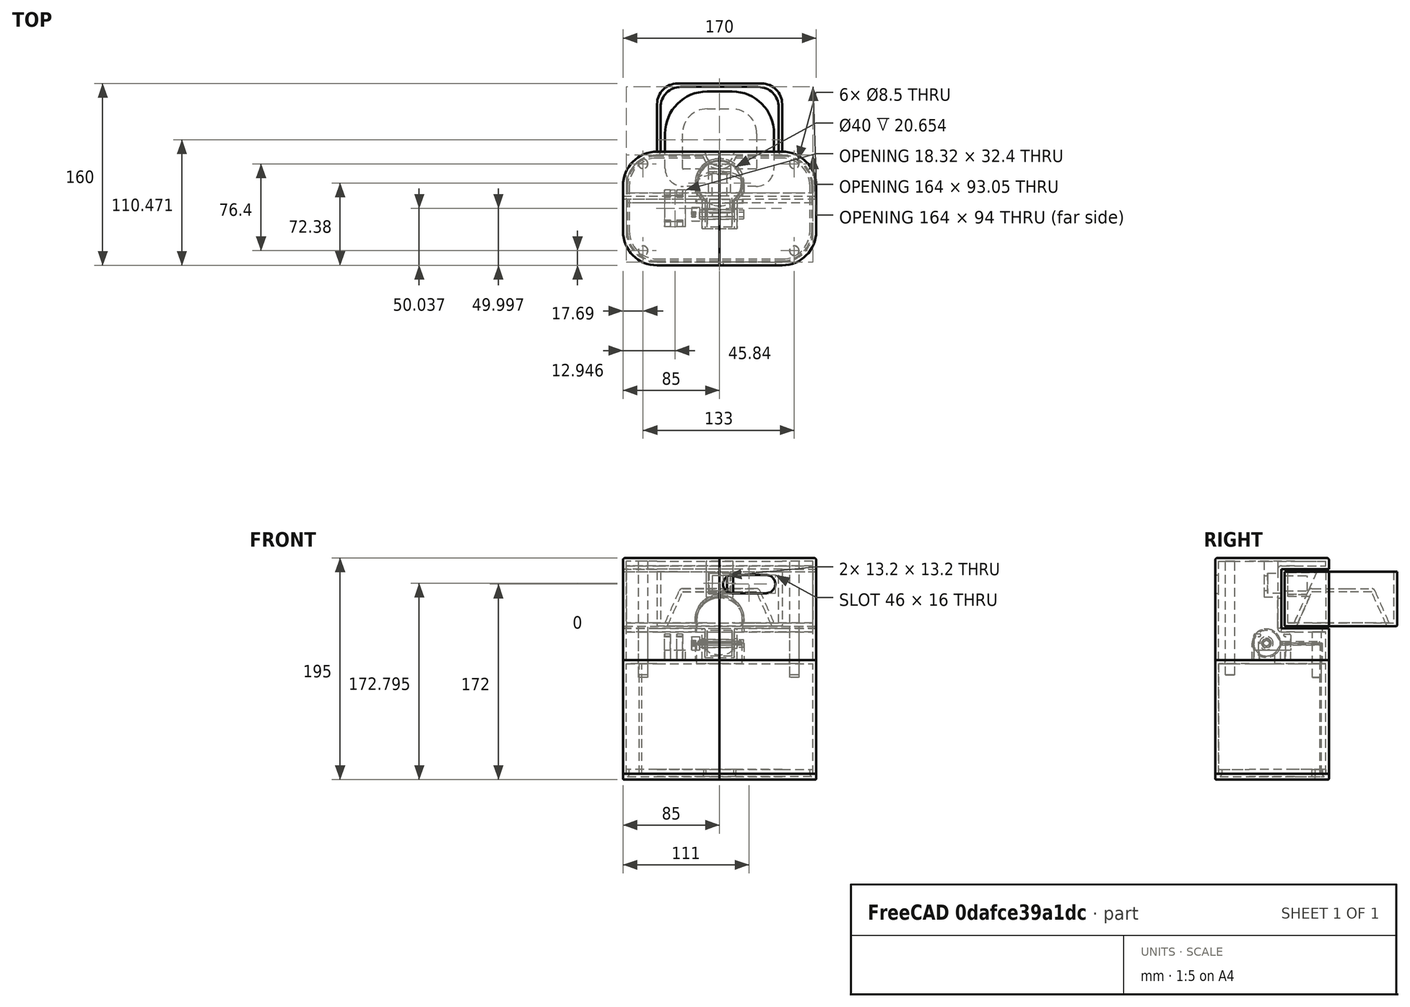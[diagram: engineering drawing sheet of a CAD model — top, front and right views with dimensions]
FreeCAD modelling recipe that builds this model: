
FCSTD DOCUMENT  (FreeCAD 1.0R39109 (Git))
Label: Feeder V3
License: All rights reserved
LicenseURL: https://en.wikipedia.org/wiki/All_rights_reserved
objects: Sketcher::SketchObject×29, PartDesign::Pocket×19, PartDesign::Pad×17, PartDesign::Fillet×8, PartDesign::ShapeBinder×8, PartDesign::Body×6, App::Link×6, PartDesign::Plane×5, PartDesign::SubShapeBinder×5, PartDesign::Thickness×4, PartDesign::Line×2, PartDesign::PolarPattern×1, PartDesign::LinearPattern×1, PartDesign::Point×1, PartDesign::Revolution×1, Part::Compound×1, Part::Box×1, Part::Cut×1, Measure::MeasureLength×1, App::DocumentObjectGroup×1
note: 239 computed .brp shape members not serialized (recipe doc carries the construction recipe); baked Part::Feature solids carry a one-line shape summary decoded from their .brp

FEATURE [Sketcher::SketchObject] Sketch
  ArcFitTolerance = 1e-06
  AttachmentSupport = -> [XY_Plane]
  FullyConstrained = true
  MakeInternals = false
  MapMode = 5
  sketch-geometry (4):
    g0: LineSegment StartX=-85 StartY=-72.3831 StartZ=0 EndX=85 EndY=-72.3831 EndZ=0
    g1: LineSegment StartX=85 StartY=-72.3831 StartZ=0 EndX=85 EndY=27.6169 EndZ=0
    g2: LineSegment StartX=85 StartY=27.6169 StartZ=0 EndX=-85 EndY=27.6169 EndZ=0
    g3: LineSegment StartX=-85 StartY=27.6169 StartZ=0 EndX=-85 EndY=-72.3831 EndZ=0
  constraints (11):
    c: Coincident(g0,g1)
    c: Coincident(g1,g2)
    c: Coincident(g2,g3)
    c: Coincident(g3,g0)
    c: Horizontal(g0)
    c: Vertical(g1)
    c: Vertical(g3)
    c: Distance(g1,g3) = 170
    c: Distance(g0,g2) = 100
    c: Symmetric(g2,g1,g-2)
    c: Block(g2)
FEATURE [PartDesign::Pad] Pad  label="Base"
  Direction = (0,0,1)
  Length = 200
  Length2 = 10
  Profile = -> Sketch
  ReferenceAxis = -> Sketch [N_Axis]
  Refine = true
  Suppressed = false
  Type = 0
FEATURE [PartDesign::Fillet] Fillet  label="Round Base Corner"
  Base = -> Pad [Edge1,Edge8,Edge2,Edge5]
  BaseFeature = -> Pad
  Radius = 30
  Refine = true
  SupportTransform = false
  Suppressed = false
  UseAllEdges = false
FEATURE [PartDesign::Thickness] Thickness
  Base = -> Fillet [Face2]
  BaseFeature = -> Fillet
  Intersection = false
  Join = 0
  Mode = 0
  Refine = true
  Reversed = true
  SupportTransform = false
  Suppressed = false
  Value = 3
FEATURE [Sketcher::SketchObject] Sketch001
  ArcFitTolerance = 1e-06
  AttachmentSupport = -> [Thickness]
  ExternalGeometry = -> [Thickness]
  FullyConstrained = true
  MakeInternals = false
  MapMode = 5
  Placement = pos=(0,0,200) rot=(0,0,1;0rad)
  sketch-geometry (7):
    g0: ArcOfCircle CenterX=0 CenterY=0 CenterZ=0 NormalX=0 NormalY=0 NormalZ=1 AngleXU=0 Radius=21.5 StartAngle=5.54716 EndAngle=10.1608
    g1: Circle CenterX=0 CenterY=0 CenterZ=0 NormalX=0 NormalY=0 NormalZ=1 AngleXU=0 Radius=20
    g2: LineSegment StartX=15.9346 StartY=-14.434 StartZ=0 EndX=15.5 EndY=-14.9137 EndZ=0
    g3: LineSegment StartX=-15.9344 StartY=-14.4341 StartZ=0 EndX=-15.5 EndY=-14.9137 EndZ=0
    g4: LineSegment StartX=-15.5 StartY=-14.9137 StartZ=0 EndX=-15.5 EndY=-39.9137 EndZ=0
    g5: LineSegment StartX=15.5 StartY=-14.9137 StartZ=0 EndX=15.5 EndY=-39.9137 EndZ=0
    g6: LineSegment StartX=-15.5 StartY=-39.9137 StartZ=0 EndX=15.5 EndY=-39.9137 EndZ=0
  constraints (16):
    c: Block(g1)
    c: Block(g0)
    c: Tangent(g0,g3) = -1.5708
    c: Tangent(g0,g2) = 1.5708
    c: Distance(g4) = 25
    c: Vertical(g4)
    c: Coincident(g4,g3)
    c: Vertical(g5)
    c: Coincident(g5,g2)
    c: Coincident(g6,g4)
    c: Coincident(g6,g5)
    c: Horizontal(g6)
    c: Diameter(g1) = 40
    c: Radius(g0) = 21.5
    c: DistanceY(g5,g5) = 25
    c: DistanceX(g6,g6) = 31
FEATURE [PartDesign::Pad] Pad001  label="DoorWay"
  BaseFeature = -> Thickness
  Direction = (0,0,1)
  Length = 15
  Length2 = 10
  Profile = -> Sketch001
  ReferenceAxis = -> Sketch001 [N_Axis]
  Refine = true
  Suppressed = false
  Type = 0
FEATURE [Sketcher::SketchObject] Sketch003
  ArcFitTolerance = 1e-06
  AttachmentSupport = -> [Pad001]
  ExternalGeometry = -> [Pad001]
  FullyConstrained = true
  MakeInternals = false
  MapMode = 5
  Placement = pos=(-15.5,0,0) rot=(0.57735,-0.57735,-0.57735;2.0944rad)
  sketch-geometry (3):
    g0: ArcOfCircle CenterX=27.4137 CenterY=215 CenterZ=0 NormalX=0 NormalY=0 NormalZ=1 AngleXU=0 Radius=12.5 StartAngle=-4.35e-14 EndAngle=3.14159
    g1: LineSegment StartX=14.9137 StartY=215 StartZ=0 EndX=27.4137 EndY=215 EndZ=0
    g2: LineSegment StartX=39.9137 StartY=215 StartZ=0 EndX=27.4137 EndY=215 EndZ=0
  constraints (9):
    c: Coincident(g0,g-3)
    c: Coincident(g0,g-3)
    c: PointOnObject(g0,g-3)
    c: PointOnObject(g1,g0)
    c: Coincident(g1,g0)
    c: Horizontal(g1)
    c: PointOnObject(g2,g0)
    c: Coincident(g2,g0)
    c: Horizontal(g2)
FEATURE [PartDesign::Pad] Pad002  label="Door Hinge Form"
  BaseFeature = -> Pad001
  Direction = (-1,0,0)
  Length = 25
  Length2 = 10
  Profile = -> Sketch003
  ReferenceAxis = -> Sketch003 [N_Axis]
  Refine = true
  Suppressed = false
  Type = 3
  UpToFace = -> Pad001 [Face23]
FEATURE [PartDesign::Pocket] Pocket  label="Pocket Container"
  BaseFeature = -> Pad002
  Direction = (0,0,-1)
  Length = 5
  Length2 = 5
  Midplane = true
  Profile = -> Pad002 [Face28]
  Refine = true
  Suppressed = false
  Type = 1
FEATURE [Sketcher::SketchObject] Sketch004
  ArcFitTolerance = 1e-06
  AttachmentSupport = -> [Pocket]
  ExternalGeometry = -> [Pocket]
  FullyConstrained = true
  MakeInternals = false
  MapMode = 5
  Placement = pos=(15.5,0,0) rot=(0.57735,0.57735,0.57735;2.0944rad)
  sketch-geometry (1):
    g0: Circle CenterX=-27.4137 CenterY=215 CenterZ=0 NormalX=0 NormalY=0 NormalZ=1 AngleXU=0 Radius=4.25
  constraints (2):
    c: Diameter(g0) = 8.5
    c: Coincident(g0,g-3)
FEATURE [PartDesign::Pocket] Pocket001  label="Pocket Hinge Circle"
  BaseFeature = -> Pocket
  Direction = (-1,0,0)
  Length = 5
  Length2 = 5
  Profile = -> Sketch004 [Edge1]
  ReferenceAxis = -> Sketch004 [N_Axis]
  Refine = true
  Suppressed = false
  Type = 1
FEATURE [Sketcher::SketchObject] Sketch009
  ArcFitTolerance = 1e-06
  AttachmentSupport = -> [YZ_Plane]
  ExternalGeometry = -> [Pocket001]
  FullyConstrained = true
  MakeInternals = false
  MapMode = 5
  Placement = pos=(0,0,0) rot=(0.57735,0.57735,0.57735;2.0944rad)
  sketch-geometry (1):
    g0: Circle CenterX=-27.4137 CenterY=215 CenterZ=0 NormalX=0 NormalY=0 NormalZ=1 AngleXU=0 Radius=12.5
  constraints (3):
    c: DistanceX(g-4,g-5) = 25
    c: Coincident(g0,g-3)
    c: PointOnObject(g-5,g0)
FEATURE [PartDesign::Pocket] Pocket004  label="Pocket Doorway form"
  BaseFeature = -> Pocket001
  Direction = (-1,0,0)
  Length = 26
  Length2 = 5
  Midplane = true
  Profile = -> Sketch009
  ReferenceAxis = -> Sketch009 [N_Axis]
  Refine = true
  Suppressed = false
  Type = 0
FEATURE [PartDesign::Line] DatumLine  label="Hinge center"
  AttacherType = Attacher::AttachEngineLine
  AttachmentSupport = -> [Pocket004]
  Length = 20
  MapMode = 42
  Placement = pos=(0,-27.4425,215) rot=(0.57735,0.57735,0.57735;2.0944rad)
  ResizeMode = 0
FEATURE [PartDesign::Plane] DatumPlane  label="Door floor plane"
  AttachmentSupport = -> [DatumLine]
  Length = 62.6838
  MapMode = 3
  Placement = pos=(0,-27.4425,215) rot=(0.707107,0.707107,0;3.14159rad)
  ResizeMode = 0
  Width = 60.2413
FEATURE [PartDesign::Plane] CopyDatumPlane
  Length = 62.6838
  Placement = pos=(-2.6041e-12,-27.4425,215) rot=(0.707107,0.707107,0;3.14159rad)
  ResizeMode = 0
  Width = 60.2413
FEATURE [PartDesign::SubShapeBinder] Binder
  BindCopyOnChange = 0
  BindMode = 0
  ClaimChildren = false
  Context = -> Body001 [Binder.]
  Fuse = false
  MakeFace = true
  OffsetFill = false
  OffsetIntersection = false
  OffsetJoinType = 0
  OffsetOpenResult = false
  PartialLoad = false
  Refine = true
  Relative = true
  Support = -> [Body[Pocket004.Edge74,Pocket004.Face29,Pocket004.Face33,Pocket004.Edge73]]
  _Version = 2
FEATURE [Sketcher::SketchObject] Sketch011
  ArcFitTolerance = 1e-06
  AttachmentSupport = -> [Binder]
  ExternalGeometry = -> [Binder]
  FullyConstrained = true
  MakeInternals = false
  MapMode = 5
  Placement = pos=(-13,0,0) rot=(0.57735,0.57735,0.57735;2.0944rad)
  sketch-geometry (7):
    g0: LineSegment StartX=-31.6637 StartY=215 StartZ=0 EndX=-29.5387 EndY=211.319 EndZ=0
    g1: LineSegment StartX=-29.5387 StartY=211.319 StartZ=0 EndX=-25.2887 EndY=211.319 EndZ=0
    g2: LineSegment StartX=-25.2887 StartY=211.319 StartZ=0 EndX=-23.1637 EndY=215 EndZ=0
    g3: LineSegment StartX=-23.1637 StartY=215 StartZ=0 EndX=-25.2887 EndY=218.681 EndZ=0
    g4: LineSegment StartX=-25.2887 StartY=218.681 StartZ=0 EndX=-29.5387 EndY=218.681 EndZ=0
    g5: LineSegment StartX=-29.5387 StartY=218.681 StartZ=0 EndX=-31.6637 EndY=215 EndZ=0
    g6: Circle [constr] CenterX=-27.4137 CenterY=215 CenterZ=0 NormalX=0 NormalY=0 NormalZ=1 AngleXU=0 Radius=4.25
  constraints (19):
    c: Coincident(g0,g1)
    c: Coincident(g1,g2)
    c: Coincident(g2,g3)
    c: Coincident(g3,g4)
    c: Coincident(g4,g5)
    c: Coincident(g5,g0)
    c: Equal(g0, g1-g5) x5
    c: PointOnObject(g0,g6)
    c: PointOnObject(g1,g6)
    c: PointOnObject(g2,g6)
    c: PointOnObject(g3,g6)
    c: PointOnObject(g4,g6)
    c: PointOnObject(g5,g6)
    c: Coincident(g6,g-5)
    c: PointOnObject(g5,g-4)
    c: Horizontal(g2,g6)
    c: DistanceX(g-5,g-6) = 59.9137
    c: DistanceX(g-6,g-6) = 34.9137
    c: DistanceX(g-5,g-6) = 25
FEATURE [Sketcher::SketchObject] Sketch012
  ArcFitTolerance = 1e-06
  AttachmentSupport = -> [YZ_Plane001]
  ExternalGeometry = -> [Binder]
  FullyConstrained = true
  MakeInternals = false
  MapMode = 5
  Placement = pos=(0,0,0) rot=(0.57735,0.57735,0.57735;2.0944rad)
  sketch-geometry (7):
    g0: ArcOfCircle CenterX=-27.4137 CenterY=215 CenterZ=0 NormalX=0 NormalY=0 NormalZ=1 AngleXU=0 Radius=11.25 StartAngle=3.14159 EndAngle=5.83678
    g1: LineSegment StartX=-15.66 StartY=213.499 StartZ=0 EndX=-17.2662 EndY=210.143 EndZ=0
    g2: ArcOfCircle CenterX=-27.4137 CenterY=215 CenterZ=0 NormalX=0 NormalY=0 NormalZ=1 AngleXU=0 Radius=11.25 StartAngle=0.444057 EndAngle=3.14159
    g3: LineSegment StartX=-15.6685 StartY=216.499 StartZ=0 EndX=-17.2548 EndY=219.833 EndZ=0
    g4: LineSegment StartX=-15.6685 StartY=216.499 StartZ=0 EndX=0 EndY=216.499 EndZ=0
    g5: LineSegment StartX=0 StartY=216.499 StartZ=0 EndX=0 EndY=213.499 EndZ=0
    g6: LineSegment StartX=-15.66 StartY=213.499 StartZ=0 EndX=0 EndY=213.499 EndZ=0
  constraints (18):
    c: Horizontal(g0,g0)
    c: Tangent(g0,g1) = 1.5708
    c: Coincident(g0,g-4)
    c: Tangent(g2,g3) = -1.5708
    c: Radius(g2) = 11.25
    c: Horizontal(g4)
    c: Coincident(g3,g4)
    c: Coincident(g0,g2)
    c: DistanceY(g0,g2) = 9.69
    c: Coincident(g5,g4)
    c: Vertical(g5)
    c: Coincident(g0,g2)
    c: PointOnObject(g4,g-2)
    c: Block(g5)
    c: DistanceX(g1,g5) = 15.66
    c: Coincident(g6,g1)
    c: Coincident(g6,g5)
    c: Horizontal(g6)
FEATURE [PartDesign::Plane] DatumPlane001  label="Door center plane"
  AttachmentSupport = -> [DatumLine]
  Length = 74.8801
  MapMode = 2
  Placement = pos=(0,-27.4425,215) rot=(0.57735,0.57735,0.57735;2.0944rad)
  ResizeMode = 0
  Width = 262.438
FEATURE [PartDesign::SubShapeBinder] Binder001
  BindCopyOnChange = 0
  BindMode = 0
  ClaimChildren = false
  Context = -> Body002 [Binder001.]
  Fuse = false
  MakeFace = true
  OffsetFill = false
  OffsetIntersection = false
  OffsetJoinType = 0
  OffsetOpenResult = false
  PartialLoad = false
  Refine = true
  Relative = true
  Support = -> [Body[Pocket004.Face23,Pocket004.Face21]]
  _Version = 2
FEATURE [PartDesign::SubShapeBinder] Binder002
  BindCopyOnChange = 0
  BindMode = 0
  ClaimChildren = false
  Context = -> Body002 [Binder002.]
  Fuse = false
  MakeFace = true
  OffsetFill = false
  OffsetIntersection = false
  OffsetJoinType = 0
  OffsetOpenResult = false
  PartialLoad = false
  Refine = true
  Relative = true
  Support = -> [Body001[Pocket006.Face3]]
  _Version = 2
FEATURE [PartDesign::Plane] CopyDatumPlane001
  Length = 74.8801
  Placement = pos=(0,-27.4425,215) rot=(0.57735,0.57735,0.57735;2.0944rad)
  ResizeMode = 0
  Width = 262.438
FEATURE [Sketcher::SketchObject] Sketch016
  ArcFitTolerance = 1e-06
  AttachmentSupport = -> [CopyDatumPlane001]
  ExternalGeometry = -> [Binder002]
  FullyConstrained = true
  MakeInternals = false
  MapMode = 5
  Placement = pos=(0,-27.4425,215) rot=(0.57735,0.57735,0.57735;2.0944rad)
  sketch-geometry (7):
    g0: LineSegment StartX=3.9 StartY=0 StartZ=0 EndX=1.95 EndY=3.3775 EndZ=0
    g1: LineSegment StartX=1.95 StartY=3.3775 StartZ=0 EndX=-1.95 EndY=3.3775 EndZ=0
    g2: LineSegment StartX=-1.95 StartY=3.3775 StartZ=0 EndX=-3.9 EndY=4.765e-13 EndZ=0
    g3: LineSegment StartX=-3.9 StartY=4.765e-13 StartZ=0 EndX=-1.95 EndY=-3.3775 EndZ=0
    g4: LineSegment StartX=-1.95 StartY=-3.3775 StartZ=0 EndX=1.95 EndY=-3.3775 EndZ=0
    g5: LineSegment StartX=1.95 StartY=-3.3775 StartZ=0 EndX=3.9 EndY=0 EndZ=0
    g6: Circle [constr] CenterX=0 CenterY=0 CenterZ=0 NormalX=0 NormalY=0 NormalZ=1 AngleXU=0 Radius=3.9
  constraints (16):
    c: Coincident(g0,g1)
    c: Coincident(g1,g2)
    c: Coincident(g2,g3)
    c: Coincident(g3,g4)
    c: Coincident(g4,g5)
    c: Coincident(g5,g0)
    c: Equal(g0, g1-g5) x5
    c: PointOnObject(g0,g6)
    c: PointOnObject(g1,g6)
    c: PointOnObject(g2,g6)
    c: PointOnObject(g3,g6)
    c: PointOnObject(g4,g6)
    c: PointOnObject(g5,g6)
    c: Radius(g6) = 3.9
    c: Coincident(g6,g-1)
    c: PointOnObject(g5,g-1)
FEATURE [PartDesign::Pad] Pad005  label="Square Push"
  Direction = (1,0,0)
  Length = 42
  Length2 = 10
  Midplane = true
  Placement = pos=(0,-27.4425,215) rot=(0.57735,0.57735,0.57735;2.0944rad)
  Profile = -> Sketch016
  ReferenceAxis = -> Sketch016 [N_Axis]
  Refine = true
  Suppressed = false
  Type = 0
FEATURE [Sketcher::SketchObject] Sketch017
  ArcFitTolerance = 1e-06
  AttachmentSupport = -> [Pad005]
  FullyConstrained = true
  MakeInternals = false
  MapMode = 5
  Placement = pos=(-21,-27.4425,215) rot=(0.57735,0.57735,-0.57735;4.18879rad)
  sketch-geometry (1):
    g0: Circle CenterX=0 CenterY=0 CenterZ=0 NormalX=0 NormalY=0 NormalZ=1 AngleXU=0 Radius=5.9
  constraints (2):
    c: Diameter(g0) = 11.8
    c: Coincident(g0,g-1)
FEATURE [PartDesign::Pad] Pad006  label="Circle push"
  BaseFeature = -> Pad005
  Direction = (-1,0,0)
  Length = 7
  Length2 = 10
  Midplane = true
  Placement = pos=(0,-27.4425,215) rot=(0.57735,0.57735,0.57735;2.0944rad)
  Profile = -> Sketch017
  ReferenceAxis = -> Sketch017 [N_Axis]
  Refine = true
  Suppressed = false
  Type = 0
FEATURE [PartDesign::SubShapeBinder] Binder003  label="Axle Binder"
  BindCopyOnChange = 0
  BindMode = 0
  ClaimChildren = false
  Context = -> Body002 [Binder003.]
  Fuse = false
  MakeFace = true
  OffsetFill = false
  OffsetIntersection = false
  OffsetJoinType = 0
  OffsetOpenResult = false
  PartialLoad = false
  Placement = pos=(3.5,-1.07e-14,0) rot=(0,0,1;0rad)
  Refine = true
  Relative = true
  _Version = 2
FEATURE [Sketcher::SketchObject] Sketch018
  ArcFitTolerance = 1e-06
  AttachmentSupport = -> [Pad006]
  ExternalGeometry = -> [Binder003]
  FullyConstrained = true
  MakeInternals = false
  MapMode = 5
  Placement = pos=(-24.5,-27.4425,215) rot=(0.57735,0.57735,-0.57735;4.18879rad)
  sketch-geometry (5):
    g0: LineSegment StartX=0 StartY=0 StartZ=0 EndX=0 EndY=2.375 EndZ=0
    g1: LineSegment StartX=0 StartY=2.375 StartZ=0 EndX=-0.0980568 EndY=2.47306 EndZ=0
    g2: LineSegment StartX=-0.0980568 StartY=2.47306 StartZ=0 EndX=-0.160985 EndY=2.46976 EndZ=0
    g3: LineSegment StartX=-0.160985 StartY=2.46976 StartZ=0 EndX=-0.248255 EndY=2.36199 EndZ=0
    g4: LineSegment StartX=-0.248255 StartY=2.36199 StartZ=0 EndX=0 EndY=0 EndZ=0
  constraints (10):
    c: Coincident(g0,g-1)
    c: Coincident(g0,g-4)
    c: Coincident(g1,g0)
    c: Coincident(g1,g-4)
    c: Coincident(g3,g2)
    c: Coincident(g3,g-5)
    c: Coincident(g4,g3)
    c: Coincident(g4,g0)
    c: Coincident(g2,g-5)
    c: Coincident(g2,g1)
FEATURE [PartDesign::Pocket] Pocket007  label="Axle form"
  BaseFeature = -> Pad006
  Direction = (1,0,0)
  Length = 3.5
  Length2 = 5
  Placement = pos=(0,-27.4425,215) rot=(0.57735,0.57735,0.57735;2.0944rad)
  Profile = -> Sketch018
  ReferenceAxis = -> Sketch018 [N_Axis]
  Refine = true
  Suppressed = false
  Type = 0
FEATURE [PartDesign::PolarPattern] PolarPattern  label="Axle repeat round"
  Angle = 360
  Axis = -> Sketch018 [N_Axis]
  BaseFeature = -> Pocket007
  Mode = 0
  Occurrences = 60
  Offset = 120
  Originals = -> [Pocket007]
  Placement = pos=(0,-27.4425,215) rot=(0.57735,0.57735,0.57735;2.0944rad)
  Refine = true
  Suppressed = false
  TransformMode = 0
FEATURE [PartDesign::Body] Body002  label="Storage Door Pin"
  AllowCompound = false
  Group = -> [Binder001,Binder002,CopyDatumPlane001,Sketch016,Pad005,Sketch017,Pad006,Sketch018,Binder003,Pocket007,PolarPattern]
  Origin = -> Origin002
  Tip = -> PolarPattern
FEATURE [Sketcher::SketchObject] Sketch020
  ArcFitTolerance = 1e-06
  AttachmentSupport = -> [Pocket004]
  ExternalGeometry = -> [Pocket004,DatumLine]
  FullyConstrained = true
  MakeInternals = false
  MapMode = 5
  Placement = pos=(0,0,200) rot=(0,0,1;0rad)
  sketch-geometry (9):
    g0: LineSegment StartX=-30 StartY=-27.4425 StartZ=0 EndX=-30 EndY=-6.14248 EndZ=0
    g1: LineSegment StartX=-30 StartY=-6.14248 StartZ=0 EndX=-32.5 EndY=-6.14248 EndZ=0
    g2: LineSegment StartX=-32.5 StartY=-6.14248 StartZ=0 EndX=-32.5 EndY=-11.0425 EndZ=0
    g3: LineSegment StartX=-32.5 StartY=-11.0425 StartZ=0 EndX=-48.3 EndY=-11.0425 EndZ=0
    g4: LineSegment StartX=-48.3 StartY=-11.0425 StartZ=0 EndX=-48.3 EndY=-33.6425 EndZ=0
    g5: LineSegment StartX=-48.3 StartY=-33.6425 StartZ=0 EndX=-32.5 EndY=-33.6425 EndZ=0
    g6: LineSegment StartX=-32.5 StartY=-33.6425 StartZ=0 EndX=-32.5 EndY=-38.5425 EndZ=0
    g7: LineSegment StartX=-30 StartY=-27.4425 StartZ=0 EndX=-30 EndY=-38.5425 EndZ=0
    g8: LineSegment StartX=-30 StartY=-38.5425 StartZ=0 EndX=-32.5 EndY=-38.5425 EndZ=0
  constraints (27):
    c: Vertical(g0)
    c: Vertical(g2)
    c: Horizontal(g3)
    c: Vertical(g4)
    c: Horizontal(g5)
    c: Vertical(g6)
    c: DistanceY(g2,g2) = 4.9
    c: DistanceY(g4,g4) = 22.6
    c: DistanceX(g5,g5) = 15.8
    c: DistanceX(g3,g3) = 15.8
    c: Coincident(g2,g3)
    c: Coincident(g0,g1)
    c: Coincident(g4,g5)
    c: Coincident(g3,g4)
    c: Coincident(g1,g2)
    c: Coincident(g6,g5)
    c: Horizontal(g1)
    c: DistanceX(g1,g1) = 2.5
    c: DistanceY(g6,g6) = 4.9
    c: Vertical(g7)
    c: Coincident(g7,g0)
    c: Coincident(g8,g7)
    c: Coincident(g8,g6)
    c: Horizontal(g8)
    c: DistanceY(g7,g7) = 11.1
    c: DistanceX(g7,g-9) = 14.5
    c: PointOnObject(g0,g-11)
FEATURE [PartDesign::Pad] Pad007  label="Servo seat"
  BaseFeature = -> Pocket004
  Direction = (0,0,1)
  Length = 8.8
  Length2 = 10
  Profile = -> Sketch020
  ReferenceAxis = -> Sketch020 [N_Axis]
  Refine = true
  Suppressed = false
  Type = 0
FEATURE [Sketcher::SketchObject] Sketch021
  ArcFitTolerance = 1e-06
  AttachmentSupport = -> [Pad007]
  ExternalGeometry = -> [Pad007,DatumLine]
  FullyConstrained = true
  MakeInternals = false
  MapMode = 5
  Placement = pos=(-32.5,0,0) rot=(0.57735,-0.57735,-0.57735;2.0944rad)
  sketch-geometry (14):
    g0: LineSegment StartX=38.5425 StartY=208.8 StartZ=0 EndX=38.5425 EndY=223 EndZ=0
    g1: LineSegment StartX=32.8474 StartY=223 StartZ=0 EndX=38.5425 EndY=223 EndZ=0
    g2: LineSegment StartX=38.5425 StartY=208.8 StartZ=0 EndX=38.5425 EndY=200 EndZ=0
    g3: LineSegment StartX=34.1425 StartY=208.69 StartZ=0 EndX=34.1425 EndY=221.1 EndZ=0
    g4: ArcOfCircle CenterX=33.4677 CenterY=222.032 CenterZ=0 NormalX=0 NormalY=0 NormalZ=1 AngleXU=0 Radius=1.15 StartAngle=2.14047 EndAngle=5.33948
    g5: LineSegment StartX=34.1425 StartY=208.69 StartZ=0 EndX=33.6425 EndY=200 EndZ=0
    g6: LineSegment StartX=33.6425 StartY=200 StartZ=0 EndX=38.5425 EndY=200 EndZ=0
    g7: LineSegment StartX=6.14248 StartY=208.8 StartZ=0 EndX=6.14248 EndY=223 EndZ=0
    g8: LineSegment StartX=11.8313 StartY=223 StartZ=0 EndX=6.14248 EndY=223 EndZ=0
    g9: LineSegment StartX=6.14248 StartY=208.8 StartZ=0 EndX=6.14248 EndY=200 EndZ=0
    g10: LineSegment StartX=10.5425 StartY=208.69 StartZ=0 EndX=10.5425 EndY=221.1 EndZ=0
    g11: ArcOfCircle CenterX=11.1278 CenterY=222.09 CenterZ=0 NormalX=0 NormalY=0 NormalZ=1 AngleXU=0 Radius=1.15 StartAngle=4.1784 EndAngle=7.19567
    g12: LineSegment StartX=10.5425 StartY=208.69 StartZ=0 EndX=11.0425 EndY=200 EndZ=0
    g13: LineSegment StartX=11.0425 StartY=200 StartZ=0 EndX=6.14248 EndY=200 EndZ=0
  constraints (36):
    c: Distance(g0) = 14.2
    c: Coincident(g0,g-3)
    c: Vertical(g0)
    c: Coincident(g1,g0)
    c: Coincident(g2,g0)
    c: Vertical(g3)
    c: Coincident(g4,g1)
    c: Coincident(g4,g3)
    c: Horizontal(g1,g0)
    c: Distance(g4,g3) = 1.15
    c: Angle(g4) = 3.19901
    c: Coincident(g5,g-5)
    c: Block(g5)
    c: Coincident(g3,g5)
    c: Coincident(g6,g5)
    c: Coincident(g6,g2)
    c: Horizontal(g6)
    c: DistanceX(g6,g6) = 4.9
    c: DistanceY(g3,g3) = 12.41
    c: Coincident(g8,g7)
    c: Coincident(g9,g7)
    c: Coincident(g11,g8)
    c: Block(g12)
    c: Coincident(g10,g12)
    c: Coincident(g13,g12)
    c: Coincident(g13,g9)
    c: Coincident(g-7,g9)
    c: Horizontal(g13)
    c: Vertical(g7)
    c: Vertical(g10)
    c: Horizontal(g8)
    c: DistanceY(g10,g10) = 12.41
    c: DistanceY(g7,g7) = 14.2
    c: DistanceX(g13,g13) = 4.9
    c: Coincident(g7,g-6)
    c: Block(g11)
FEATURE [PartDesign::Pad] Pad008  label="ServoHolder"
  BaseFeature = -> Pad007
  Direction = (-1,0,0)
  Length = 5
  Length2 = 10
  Profile = -> Sketch021
  ReferenceAxis = -> Sketch021 [N_Axis]
  Refine = true
  Suppressed = false
  Type = 0
FEATURE [PartDesign::LinearPattern] LinearPattern  label="Clip repeat"
  BaseFeature = -> Pad008
  Direction = -> Pad008 [Face21]
  Length = 10.82
  Mode = 0
  Occurrences = 2
  Offset = 10.82
  Originals = -> [Pad008]
  Refine = true
  Reversed = true
  Suppressed = false
  TransformMode = 0
FEATURE [PartDesign::Plane] DatumPlane002  label="Floor storage"
  AttachmentSupport = -> [LinearPattern]
  Length = 60
  MapMode = 5
  Placement = pos=(0,0,200) rot=(0,0,1;0rad)
  ResizeMode = 0
  Width = 60
FEATURE [PartDesign::SubShapeBinder] Binder004
  BindCopyOnChange = 0
  BindMode = 0
  ClaimChildren = false
  Context = -> Body [Binder004.]
  Fuse = false
  MakeFace = true
  OffsetFill = false
  OffsetIntersection = false
  OffsetJoinType = 0
  OffsetOpenResult = false
  PartialLoad = false
  Refine = true
  Relative = true
  Support = -> [LinearPattern[Face2]]
  _Version = 2
FEATURE [PartDesign::Pocket] Pocket008
  BaseFeature = -> LinearPattern
  Direction = (0,0,1)
  Length = 100
  Length2 = 5
  Profile = -> Binder004
  Refine = true
  Suppressed = false
  Type = 0
FEATURE [PartDesign::ShapeBinder] ShapeBinder001  label="Base Shape Binder"
  Support = -> [Pocket008]
  TraceSupport = false
FEATURE [PartDesign::Pad] Pad015  label="Height of base"
  Direction = (0,0,1)
  Length = 90
  Length2 = 10
  Profile = -> ShapeBinder001
  Refine = true
  Suppressed = false
  Type = 0
FEATURE [PartDesign::ShapeBinder] CopyPocket009  label="Storage Door Datum"
  Placement = pos=(0,0,215) rot=(0,0,1;0rad)
  TraceSupport = false
FEATURE [PartDesign::Line] DatumLine001  label="Storage Door Center"
  AttacherType = Attacher::AttachEngineLine
  AttachmentSupport = -> [CopyPocket009]
  Length = 20
  MapMode = 19
  Placement = pos=(0,0,215) rot=(0,0,-1;0.736025rad)
  ResizeMode = 0
FEATURE [PartDesign::Point] DatumPoint001  label="Storage Door Axle"
  AttacherType = Attacher::AttachEnginePoint
  AttachmentSupport = -> [Pocket008]
  MapMode = 36
  Placement = pos=(-15.5,-27.4137,215) rot=(0.707107,0.707107,0;3.14159rad)
FEATURE [Sketcher::SketchObject] Sketch034
  ArcFitTolerance = 1e-06
  AttachmentSupport = -> [Pad015]
  ExternalGeometry = -> [DatumPoint001,CopyPocket009,Pad015]
  FullyConstrained = true
  MakeInternals = false
  MapMode = 5
  Placement = pos=(85,0,0) rot=(0.57735,0.57735,0.57735;2.0944rad)
  sketch-geometry (4):
    g0: LineSegment StartX=84.996 StartY=228 StartZ=0 EndX=84.996 EndY=280 EndZ=0
    g1: LineSegment StartX=84.996 StartY=280 StartZ=0 EndX=-14.434 EndY=280 EndZ=0
    g2: LineSegment StartX=-14.434 StartY=280 StartZ=0 EndX=-14.434 EndY=228 EndZ=0
    g3: LineSegment StartX=-14.434 StartY=228 StartZ=0 EndX=84.996 EndY=228 EndZ=0
  constraints (12):
    c: Coincident(g0,g1)
    c: Coincident(g1,g2)
    c: Coincident(g2,g3)
    c: Coincident(g3,g0)
    c: Vertical(g0)
    c: Vertical(g2)
    c: Horizontal(g1)
    c: Horizontal(g3)
    c: DistanceY(g2,g2) = 52
    c: PointOnObject(g-4,g2)
    c: Distance(g-6,g1) = 10
    c: DistanceX(g3,g3) = 99.43
FEATURE [PartDesign::ShapeBinder] CopyPocket010  label="Hinge length"
  Placement = pos=(0,0,215) rot=(0,0,1;0rad)
  TraceSupport = false
FEATURE [PartDesign::Pocket] Pocket009  label="Food Plate Cut"
  BaseFeature = -> Pad015
  Direction = (-1,0,0)
  Length = 0
  Length2 = 5
  Profile = -> Sketch034
  ReferenceAxis = -> Sketch034 [N_Axis]
  Refine = true
  Suppressed = false
  Type = 3
  UpToFace = -> Pad015 [Face3]
FEATURE [PartDesign::Thickness] Thickness001
  Base = -> Pocket009 [Face2]
  BaseFeature = -> Pocket009
  Intersection = false
  Join = 0
  Mode = 0
  Refine = true
  Reversed = true
  SupportTransform = false
  Suppressed = false
  Value = 3
FEATURE [Sketcher::SketchObject] Sketch037
  ArcFitTolerance = 1e-06
  AttachmentSupport = -> [Thickness001]
  ExternalGeometry = -> [CopyPocket009]
  FullyConstrained = true
  MakeInternals = false
  MapMode = 5
  Placement = pos=(0,0,225) rot=(1,0,0;3.14159rad)
  sketch-geometry (6):
    g0: ArcOfCircle CenterX=0 CenterY=0 CenterZ=0 NormalX=0 NormalY=0 NormalZ=1 AngleXU=0 Radius=21.5 StartAngle=3.0286 EndAngle=6.39618
    g1: LineSegment StartX=20 StartY=34.4342 StartZ=0 EndX=20 EndY=14.4342 EndZ=0
    g2: LineSegment StartX=-20 StartY=34.4342 StartZ=0 EndX=-20 EndY=14.4342 EndZ=0
    g3: ArcOfCircle CenterX=3.5332e-12 CenterY=-35.523 CenterZ=0 NormalX=0 NormalY=0 NormalZ=1 AngleXU=0 Radius=72.76 StartAngle=1.29234 EndAngle=1.84926
    g4: LineSegment StartX=20 StartY=14.4342 StartZ=0 EndX=21.3629 EndY=2.42425 EndZ=0
    g5: LineSegment StartX=-20 StartY=14.4342 StartZ=0 EndX=-21.3629 EndY=2.42425 EndZ=0
  constraints (19):
    c: Coincident(g0,g-1)
    c: Coincident(g3,g2)
    c: Coincident(g1,g3)
    c: DistanceX(g-6,g2) = 3
    c: DistanceX(g1,g-5) = 3
    c: Vertical(g2,g2)
    c: Horizontal(g2,g1)
    c: Radius(g3) = 72.76
    c: Tangent(g0,g5) = -1.5708
    c: Radius(g0) = 21.5
    c: Coincident(g5,g2)
    c: Tangent(g0,g4) = 1.5708
    c: Coincident(g1,g4)
    c: Horizontal(g1,g2)
    c: Vertical(g1)
    c: DistanceY(g5,g5) = 12.01
    c: DistanceY(g4,g4) = 12.01
    c: DistanceY(g1,g1) = 20
    c: DistanceY(g-5,g-5) = 23
FEATURE [PartDesign::Pocket] Pocket010  label="Food door cut"
  BaseFeature = -> Thickness001
  Direction = (0,0,1)
  Length = 0
  Length2 = 5
  Profile = -> Sketch037
  ReferenceAxis = -> Sketch037 [N_Axis]
  Refine = true
  Suppressed = false
  Type = 3
  UpToFace = -> Thickness001 [Face3]
FEATURE [PartDesign::Pad] Pad019  label="Door Pin width"
  Direction = (1,0,0)
  Length = 22
  Length2 = 10
  Midplane = true
  Placement = pos=(0,0,0) rot=(1,1,1;2.0944rad)
  Profile = -> Sketch012
  ReferenceAxis = -> Sketch012 [N_Axis]
  Refine = true
  Suppressed = false
  Type = 0
FEATURE [Sketcher::SketchObject] Sketch015
  ArcFitTolerance = 1e-06
  AttachmentSupport = -> [Pad019]
  FullyConstrained = true
  MakeInternals = false
  MapMode = 5
  Placement = pos=(0,4.76e-14,216.499) rot=(0,0,-1;1.5708rad)
  sketch-geometry (5):
    g0: LineSegment StartX=1.545e-13 StartY=-11 StartZ=0 EndX=1.616e-13 EndY=11 EndZ=0
    g1: LineSegment StartX=1.616e-13 StartY=11 StartZ=0 EndX=15.6637 EndY=11 EndZ=0
    g2: LineSegment StartX=1.545e-13 StartY=-11 StartZ=0 EndX=15.6637 EndY=-11 EndZ=0
    g3: LineSegment StartX=15.6637 StartY=11 StartZ=0 EndX=0 EndY=1.8e-15 EndZ=0
    g4: LineSegment StartX=0 StartY=1.8e-15 StartZ=0 EndX=15.6637 EndY=-11 EndZ=0
  constraints (10):
    c: Coincident(g0,g-4)
    c: Coincident(g0,g-6)
    c: Coincident(g1,g0)
    c: Coincident(g1,g-6)
    c: Coincident(g2,g0)
    c: Coincident(g2,g-5)
    c: Coincident(g3,g-6)
    c: Coincident(g3,g-1)
    c: Coincident(g4,g3)
    c: Coincident(g4,g2)
FEATURE [PartDesign::Pocket] Pocket014  label="Door Cut"
  BaseFeature = -> Pad019
  Direction = (0,0,-1)
  Length = 0
  Length2 = 5
  Placement = pos=(0,0,0) rot=(1,1,1;2.0944rad)
  Profile = -> Sketch015
  ReferenceAxis = -> Sketch015 [N_Axis]
  Refine = true
  Suppressed = false
  Type = 3
  UpToFace = -> Pad019 [Face2]
FEATURE [PartDesign::Pocket] Pocket015  label="Door Pin Hole"
  BaseFeature = -> Pocket014
  Direction = (-1,0,0)
  Length = 5
  Length2 = 5
  Placement = pos=(0,0,0) rot=(1,1,1;2.0944rad)
  Profile = -> Sketch011
  ReferenceAxis = -> Sketch011 [N_Axis]
  Refine = true
  Reversed = true
  Suppressed = false
  Type = 1
FEATURE [PartDesign::Revolution] Revolution
  Angle = 360
  Angle2 = 60
  Axis = (7e-16,-2e-16,-1)
  Base = (-1.665e-13,1.202e-13,216.499)
  BaseFeature = -> Pocket015
  Placement = pos=(0,0,0) rot=(1,1,1;2.0944rad)
  Profile = -> Pocket015 [Face8]
  ReferenceAxis = -> Pocket015 [Edge37]
  Refine = true
  Suppressed = false
  Type = 3
  UpToFace = -> Pocket015 [Face9]
FEATURE [PartDesign::Fillet] Fillet001
  Base = -> Revolution [Edge32,Edge1]
  BaseFeature = -> Revolution
  Placement = pos=(0,0,0) rot=(1,1,1;2.0944rad)
  Radius = 4
  Refine = true
  SupportTransform = false
  Suppressed = false
  UseAllEdges = false
FEATURE [PartDesign::Body] Body001  label="Storage Door"
  AllowCompound = false
  Group = -> [CopyDatumPlane,Binder,Sketch011,Sketch012,Sketch015,Pad019,Pocket014,Pocket015,Revolution,Fillet001]
  Origin = -> Origin001
  Tip = -> Fillet001
FEATURE [Sketcher::SketchObject] Sketch054
  ArcFitTolerance = 1e-06
  AttachmentSupport = -> [Pocket010]
  ExternalGeometry = -> [Pocket010]
  FullyConstrained = true
  MakeInternals = false
  MapMode = 5
  Placement = pos=(0,-14.434,0) rot=(0,0.707107,0.707107;3.14159rad)
  sketch-geometry (1):
    g0: Circle CenterX=-3.5467e-12 CenterY=233.933 CenterZ=0 NormalX=0 NormalY=0 NormalZ=1 AngleXU=0 Radius=20.8615
  constraints (3):
    c: PointOnObject(g-3,g0)
    c: PointOnObject(g-3,g0)
    c: Block(g0)
FEATURE [PartDesign::Pocket] Pocket024  label="Food door cut001"
  BaseFeature = -> Pocket010
  Direction = (0,-1,2e-16)
  Length = 0
  Length2 = 5
  Profile = -> Sketch054
  ReferenceAxis = -> Sketch054 [N_Axis]
  Refine = true
  Suppressed = false
  Type = 3
  UpToFace = -> Pocket010 [Face32]
FEATURE [PartDesign::ShapeBinder] CopyPocket017  label="Food base form"
  Support = -> [Pocket024]
  TraceSupport = false
FEATURE [Sketcher::SketchObject] Sketch048
  ArcFitTolerance = 1e-06
  AttachmentSupport = -> [CopyPocket017]
  ExternalGeometry = -> [CopyPocket017]
  FullyConstrained = true
  MakeInternals = false
  MapMode = 5
  Placement = pos=(0,0,280) rot=(1,0,0;3.14159rad)
  sketch-geometry (8):
    g0: ArcOfCircle CenterX=-55 CenterY=2.38314 CenterZ=0 NormalX=0 NormalY=0 NormalZ=1 AngleXU=1.5708 Radius=30 StartAngle=1.5708 EndAngle=3.14159
    g1: LineSegment StartX=-55 StartY=-27.6169 StartZ=0 EndX=-55 EndY=-87.6169 EndZ=0
    g2: LineSegment StartX=-55 StartY=-87.6169 StartZ=0 EndX=55 EndY=-87.6169 EndZ=0
    g3: ArcOfCircle CenterX=55 CenterY=2.38314 CenterZ=0 NormalX=0 NormalY=0 NormalZ=1 AngleXU=1.5708 Radius=30 StartAngle=3.14159 EndAngle=4.71239
    g4: LineSegment StartX=55 StartY=-27.6169 StartZ=0 EndX=55 EndY=-87.6169 EndZ=0
    g5: LineSegment StartX=-85 StartY=2.38314 StartZ=0 EndX=-85 EndY=11.434 EndZ=0
    g6: LineSegment StartX=-85 StartY=11.434 StartZ=0 EndX=85 EndY=11.434 EndZ=0
    g7: LineSegment StartX=85 StartY=2.38314 StartZ=0 EndX=85 EndY=11.434 EndZ=0
  constraints (22):
    c: Coincident(g0,g-5)
    c: Coincident(g1,g2)
    c: Vertical(g1)
    c: Horizontal(g2)
    c: Distance(g2,g1) = 60
    c: Coincident(g1,g0)
    c: DistanceX(g2,g2) = 110
    c: Horizontal(g-5,g3)
    c: Vertical(g0,g-5)
    c: Coincident(g3,g-6)
    c: Block(g3)
    c: Coincident(g4,g3)
    c: Coincident(g4,g2)
    c: Coincident(g5,g0)
    c: PointOnObject(g5,g-3)
    c: Coincident(g6,g5)
    c: Horizontal(g6)
    c: Coincident(g7,g3)
    c: Coincident(g7,g6)
    c: Vertical(g7)
    c: Distance(g5,g-4) = 3
    c: Coincident(g0,g-5)
FEATURE [PartDesign::Pad] Pad024  label="Plate height"
  Direction = (0,0,-1)
  Length = 50
  Length2 = 10
  Profile = -> Sketch048
  ReferenceAxis = -> Sketch048 [N_Axis]
  Refine = true
  Suppressed = false
  Type = 0
FEATURE [Sketcher::SketchObject] Sketch050
  ArcFitTolerance = 1e-06
  AttachmentSupport = -> [Pad024]
  ExternalGeometry = -> [Pad024]
  FullyConstrained = true
  MakeInternals = false
  MapMode = 5
  Placement = pos=(0,0,230) rot=(1,0,0;3.14159rad)
  sketch-geometry (13):
    g0: LineSegment StartX=-46 StartY=-13.0173 StartZ=0 EndX=-46 EndY=-43.6291 EndZ=0
    g1: LineSegment StartX=-11.0122 StartY=-78.6169 StartZ=0 EndX=11.0122 EndY=-78.6169 EndZ=0
    g2: LineSegment StartX=46 StartY=-43.6291 StartZ=0 EndX=46 EndY=-13.0173 EndZ=0
    g3: LineSegment StartX=32.0488 StartY=0.933964 StartZ=0 EndX=-32.0488 EndY=0.933964 EndZ=0
    g4: GeomPoint [constr] X=0 Y=-38.8414 Z=0
    g5: ArcOfCircle CenterX=11.0122 CenterY=-43.6291 CenterZ=0 NormalX=0 NormalY=0 NormalZ=1 AngleXU=0 Radius=34.9878 StartAngle=4.71239 EndAngle=6.28319
    g6: GeomPoint [constr] X=46 Y=-78.6169 Z=0
    g7: ArcOfCircle CenterX=-11.0122 CenterY=-43.6291 CenterZ=0 NormalX=0 NormalY=0 NormalZ=1 AngleXU=0 Radius=34.9878 StartAngle=3.14159 EndAngle=4.71239
    g8: GeomPoint [constr] X=-46 Y=-78.6169 Z=0
    g9: ArcOfCircle CenterX=32.0488 CenterY=-13.0173 CenterZ=0 NormalX=0 NormalY=0 NormalZ=1 AngleXU=0 Radius=13.9512 StartAngle=-1.652e-13 EndAngle=1.5708
    g10: GeomPoint [constr] X=46 Y=0.933964 Z=0
    g11: ArcOfCircle CenterX=-32.0488 CenterY=-13.0173 CenterZ=0 NormalX=0 NormalY=0 NormalZ=1 AngleXU=0 Radius=13.9512 StartAngle=1.5708 EndAngle=3.14159
    g12: GeomPoint [constr] X=-46 Y=0.933964 Z=0
  constraints (29):
    c: Vertical(g0)
    c: Vertical(g2)
    c: Horizontal(g1)
    c: Horizontal(g3)
    c: Symmetric(g6,g12,g4)
    c: PointOnObject(g4,g-2)
    c: Distance(g-4,g2) = 9
    c: Distance(g10,g-3) = 12
    c: PointOnObject(g6,g1)
    c: PointOnObject(g6,g2)
    c: Tangent(g1,g5) = -1.5708
    c: Tangent(g2,g5) = -1.5708
    c: PointOnObject(g8,g0)
    c: PointOnObject(g8,g1)
    c: Tangent(g0,g7) = -1.5708
    c: Tangent(g1,g7) = -1.5708
    c: PointOnObject(g10,g2)
    c: PointOnObject(g10,g3)
    c: Tangent(g2,g9) = -1.5708
    c: Tangent(g3,g9) = -1.5708
    c: PointOnObject(g12,g0)
    c: PointOnObject(g12,g3)
    c: Tangent(g0,g11) = -1.5708
    c: Tangent(g3,g11) = -1.5708
    c: Distance(g-6,g1) = 9
    c: Horizontal(g7,g5)
    c: Block(g7)
    c: Horizontal(g11,g9)
    c: Block(g11)
FEATURE [PartDesign::Pocket] Pocket025  label="Plate Bowl cut"
  BaseFeature = -> Pad024
  Direction = (0,0,1)
  Length = 30
  Length2 = 5
  Profile = -> Sketch050
  ReferenceAxis = -> Sketch050 [N_Axis]
  Refine = true
  Suppressed = false
  TaperAngle = -24
  Type = 0
FEATURE [Sketcher::SketchObject] Sketch052
  ArcFitTolerance = 1e-06
  AttachmentSupport = -> [Pocket025]
  FullyConstrained = true
  MakeInternals = false
  MapMode = 5
  Placement = pos=(0,-11.434,0) rot=(1,0,0;1.5708rad)
  sketch-geometry (2):
    g0: ArcOfCircle CenterX=0 CenterY=236.136 CenterZ=0 NormalX=0 NormalY=0 NormalZ=1 AngleXU=0 Radius=21.5 StartAngle=5.99378 EndAngle=9.71418
    g1: LineSegment StartX=-20.6059 StartY=230 StartZ=0 EndX=20.6059 EndY=230 EndZ=0
  constraints (6):
    c: Coincident(g0,g-3)
    c: Diameter(g0) = 43
    c: PointOnObject(g1,g-4)
    c: Horizontal(g1)
    c: Coincident(g0,g1)
    c: Coincident(g0,g1)
FEATURE [PartDesign::Thickness] Thickness002
  Base = -> Pocket025 [Face4]
  BaseFeature = -> Pocket025
  Intersection = false
  Join = 0
  Mode = 0
  Refine = true
  Reversed = true
  SupportTransform = false
  Suppressed = false
  Value = 3
FEATURE [PartDesign::Pad] Pad025
  BaseFeature = -> Thickness002
  Direction = (0,-1,2e-16)
  Length = 10
  Length2 = 10
  Profile = -> Sketch052
  ReferenceAxis = -> Sketch052 [N_Axis]
  Refine = true
  Suppressed = false
  Type = 3
  UpToFace = -> Thickness002 [Face43]
FEATURE [Sketcher::SketchObject] Sketch055
  ArcFitTolerance = 1e-06
  AttachmentSupport = -> [Pad025]
  ExternalGeometry = -> [Sketch052]
  FullyConstrained = true
  MakeInternals = false
  MapMode = 5
  Placement = pos=(0,-11.434,0) rot=(1,0,0;1.5708rad)
  sketch-geometry (1):
    g0: Circle CenterX=0 CenterY=236.136 CenterZ=0 NormalX=0 NormalY=0 NormalZ=1 AngleXU=0 Radius=20
  constraints (2):
    c: Coincident(g0,g-3)
    c: Diameter(g0) = 40
FEATURE [PartDesign::Pocket] Pocket026
  BaseFeature = -> Pad025
  Direction = (0,1,-2e-16)
  Length = 0
  Length2 = 5
  Profile = -> Sketch055
  ReferenceAxis = -> Sketch055 [N_Axis]
  Refine = true
  Suppressed = false
  Type = 3
  UpToFace = -> Pad025 [Face41]
FEATURE [PartDesign::Fillet] Fillet002
  Base = -> Pocket026 [Edge101,Edge65,Edge67,Edge99]
  BaseFeature = -> Pocket026
  Radius = 18
  Refine = true
  SupportTransform = false
  Suppressed = false
  UseAllEdges = false
FEATURE [Sketcher::SketchObject] Sketch056  label="HX711 Hole"
  ArcFitTolerance = 1e-06
  AttachmentSupport = -> [Pocket024]
  ExternalGeometry = -> [DatumLine001,Pocket024]
  FullyConstrained = true
  MakeInternals = false
  MapMode = 5
  Placement = pos=(0,-14.434,0) rot=(0,0.707107,0.707107;3.14159rad)
  sketch-geometry (10):
    g0: LineSegment StartX=-9 StartY=276.795 StartZ=0 EndX=-9 EndY=258.795 EndZ=0
    g1: LineSegment StartX=-9 StartY=258.795 StartZ=0 EndX=9 EndY=258.795 EndZ=0
    g2: LineSegment StartX=9 StartY=258.795 StartZ=0 EndX=9 EndY=276.795 EndZ=0
    g3: LineSegment StartX=9 StartY=276.795 StartZ=0 EndX=-9 EndY=276.795 EndZ=0
    g4: GeomPoint [constr] X=2.1e-15 Y=267.795 Z=0
    g5: LineSegment StartX=6.6 StartY=261.195 StartZ=0 EndX=6.6 EndY=274.395 EndZ=0
    g6: LineSegment StartX=6.6 StartY=274.395 StartZ=0 EndX=-6.6 EndY=274.395 EndZ=0
    g7: LineSegment StartX=-6.6 StartY=274.395 StartZ=0 EndX=-6.6 EndY=261.195 EndZ=0
    g8: LineSegment StartX=-6.6 StartY=261.195 StartZ=0 EndX=6.6 EndY=261.195 EndZ=0
    g9: GeomPoint [constr] X=2.1e-15 Y=267.795 Z=0
  constraints (25):
    c: Coincident(g0,g1)
    c: Coincident(g1,g2)
    c: Coincident(g2,g3)
    c: Coincident(g3,g0)
    c: Vertical(g0)
    c: Vertical(g2)
    c: Horizontal(g1)
    c: Horizontal(g3)
    c: Symmetric(g2,g0,g4)
    c: PointOnObject(g4,g-3)
    c: DistanceX(g3,g3) = 18
    c: DistanceY(g0,g0) = 18
    c: Distance(g-4,g1) = 4
    c: Coincident(g5,g6)
    c: Coincident(g6,g7)
    c: Coincident(g7,g8)
    c: Coincident(g8,g5)
    c: Vertical(g5)
    c: Vertical(g7)
    c: Horizontal(g6)
    c: Horizontal(g8)
    c: Symmetric(g7,g5,g9)
    c: Coincident(g9,g4)
    c: DistanceX(g8,g8) = 13.2
    c: DistanceY(g7,g7) = 13.2
FEATURE [Sketcher::SketchObject] Sketch057
  ArcFitTolerance = 1e-06
  AttachmentSupport = -> [Pocket024]
  ExternalGeometry = -> [Sketch056,Pocket024]
  FullyConstrained = true
  MakeInternals = false
  MapMode = 5
  Placement = pos=(0,-17.434,0) rot=(1,0,0;1.5708rad)
  sketch-geometry (4):
    g0: LineSegment StartX=-12 StartY=290 StartZ=0 EndX=-12 EndY=255.795 EndZ=0
    g1: LineSegment StartX=-12 StartY=255.795 StartZ=0 EndX=12 EndY=255.795 EndZ=0
    g2: LineSegment StartX=12 StartY=255.795 StartZ=0 EndX=12 EndY=290 EndZ=0
    g3: LineSegment StartX=12 StartY=290 StartZ=0 EndX=-12 EndY=290 EndZ=0
  constraints (11):
    c: Coincident(g0,g1)
    c: Coincident(g1,g2)
    c: Coincident(g2,g3)
    c: Coincident(g3,g0)
    c: Vertical(g0)
    c: Vertical(g2)
    c: Horizontal(g1)
    c: PointOnObject(g0,g-4)
    c: Distance(g1,g-5) = 3
    c: Symmetric(g0,g2,g-2)
    c: Distance(g0,g-6) = 3
FEATURE [PartDesign::Pad] Pad026  label="HX71 Hole width"
  BaseFeature = -> Pocket024
  Direction = (0,-1,2e-16)
  Length = 12
  Length2 = 10
  Profile = -> Sketch057
  ReferenceAxis = -> Sketch057 [N_Axis]
  Refine = true
  Suppressed = false
  Type = 0
FEATURE [PartDesign::Pocket] Pocket027
  BaseFeature = -> Pad026
  Direction = (0,-1,2e-16)
  Length = 0
  Length2 = 5
  Profile = -> Sketch056 [Edge7,Edge8,Edge5,Edge6]
  ReferenceAxis = -> Sketch056 [N_Axis]
  Refine = true
  Suppressed = false
  Type = 3
  UpToFace = -> Pad026 [Face40]
FEATURE [PartDesign::ShapeBinder] ShapeBinder  label="HX711 Hole Binder"
  Support = -> [Pocket027]
  TraceSupport = false
FEATURE [Sketcher::SketchObject] Sketch058
  ArcFitTolerance = 1e-06
  AttachmentSupport = -> [Fillet002]
  ExternalGeometry = -> [ShapeBinder]
  FullyConstrained = true
  MakeInternals = false
  MapMode = 5
  Placement = pos=(0,-8.43396,0) rot=(0,0.707107,0.707107;3.14159rad)
  sketch-geometry (4):
    g0: LineSegment StartX=-9.6 StartY=258.195 StartZ=0 EndX=9.6 EndY=258.195 EndZ=0
    g1: LineSegment StartX=9.6 StartY=258.195 StartZ=0 EndX=9.6 EndY=277.395 EndZ=0
    g2: LineSegment StartX=9.6 StartY=277.395 StartZ=0 EndX=-9.6 EndY=277.395 EndZ=0
    g3: LineSegment StartX=-9.6 StartY=277.395 StartZ=0 EndX=-9.6 EndY=258.195 EndZ=0
  constraints (12):
    c: Coincident(g0,g1)
    c: Coincident(g1,g2)
    c: Coincident(g2,g3)
    c: Coincident(g3,g0)
    c: Horizontal(g0)
    c: Horizontal(g2)
    c: Vertical(g1)
    c: Vertical(g3)
    c: Distance(g3,g-5) = 3
    c: Distance(g0,g-3) = 3
    c: Distance(g1,g-4) = 3
    c: Distance(g2,g-6) = 3
FEATURE [PartDesign::Pad] Pad027
  BaseFeature = -> Fillet002
  Direction = (0,1,-2e-16)
  Length = 10
  Length2 = 10
  Profile = -> Sketch058
  ReferenceAxis = -> Sketch058 [N_Axis]
  Refine = true
  Suppressed = false
  Type = 3
  UpToFace = -> Fillet002 [Face14]
FEATURE [Sketcher::SketchObject] Sketch059
  ArcFitTolerance = 1e-06
  AttachmentSupport = -> [Pad027]
  ExternalGeometry = -> [ShapeBinder]
  FullyConstrained = true
  MakeInternals = false
  MapMode = 5
  Placement = pos=(0,-11.434,0) rot=(1,0,0;1.5708rad)
  sketch-geometry (4):
    g0: LineSegment StartX=-6.6 StartY=274.395 StartZ=0 EndX=-6.6 EndY=261.195 EndZ=0
    g1: LineSegment StartX=-6.6 StartY=261.195 StartZ=0 EndX=6.6 EndY=261.195 EndZ=0
    g2: LineSegment StartX=6.6 StartY=261.195 StartZ=0 EndX=6.6 EndY=274.395 EndZ=0
    g3: LineSegment StartX=6.6 StartY=274.395 StartZ=0 EndX=-6.6 EndY=274.395 EndZ=0
  constraints (10):
    c: Coincident(g0,g1)
    c: Coincident(g1,g2)
    c: Coincident(g2,g3)
    c: Coincident(g3,g0)
    c: Vertical(g0)
    c: Vertical(g2)
    c: Horizontal(g1)
    c: Horizontal(g3)
    c: Coincident(g0,g-5)
    c: Coincident(g1,g-6)
FEATURE [PartDesign::Pocket] Pocket028
  BaseFeature = -> Pad027
  Direction = (0,1,-2e-16)
  Length = 20
  Length2 = 5
  Profile = -> Sketch059
  ReferenceAxis = -> Sketch059 [N_Axis]
  Refine = true
  Suppressed = false
  Type = 0
FEATURE [Sketcher::SketchObject] Sketch060
  ArcFitTolerance = 1e-06
  AttachmentSupport = -> [Pocket027]
  ExternalGeometry = -> [Pocket027]
  FullyConstrained = true
  MakeInternals = false
  MapMode = 5
  Placement = pos=(0,-72.3831,0) rot=(1,0,0;1.5708rad)
  sketch-geometry (4):
    g0: ArcOfCircle CenterX=41 CenterY=267 CenterZ=0 NormalX=0 NormalY=0 NormalZ=1 AngleXU=0 Radius=8 StartAngle=4.71239 EndAngle=7.85398
    g1: ArcOfCircle CenterX=11 CenterY=267 CenterZ=0 NormalX=0 NormalY=0 NormalZ=1 AngleXU=0 Radius=8 StartAngle=1.5708 EndAngle=4.71239
    g2: LineSegment StartX=41 StartY=259 StartZ=0 EndX=11 EndY=259 EndZ=0
    g3: LineSegment StartX=41 StartY=275 StartZ=0 EndX=11 EndY=275 EndZ=0
  constraints (10):
    c: Tangent(g0,g2) = 1.5708
    c: Tangent(g0,g3) = -1.5708
    c: Tangent(g1,g2) = 1.5708
    c: Tangent(g1,g3) = -1.5708
    c: Equal(g0,g1)
    c: Horizontal(g3)
    c: Distance(g0,g1) = 30
    c: Radius(g0) = 8
    c: Distance(g-3,g3) = 15
    c: Distance(g0,g-5) = 6
FEATURE [PartDesign::Pocket] Pocket030
  BaseFeature = -> Pocket027
  Direction = (0,1,-2e-16)
  Length = 0
  Length2 = 5
  Profile = -> Sketch060
  ReferenceAxis = -> Sketch060 [N_Axis]
  Refine = true
  Suppressed = false
  Type = 3
  UpToFace = -> Pocket027 [Face15]
FEATURE [PartDesign::ShapeBinder] ShapeBinder002  label="Inside Base Shape"
  Support = -> [Pocket008]
  TraceSupport = false
FEATURE [PartDesign::ShapeBinder] ShapeBinder003  label="Outside Shape"
  Support = -> [Pocket008]
  TraceSupport = false
FEATURE [PartDesign::Pad] Pad028
  Direction = (0,0,1)
  Length = 4
  Length2 = 10
  Profile = -> ShapeBinder002
  Refine = true
  Suppressed = false
  Type = 0
FEATURE [PartDesign::Pad] Pad029
  BaseFeature = -> Pad028
  Direction = (0,0,1)
  Length = 5
  Length2 = 10
  Profile = -> ShapeBinder003
  Refine = true
  Reversed = true
  Suppressed = false
  Type = 0
FEATURE [Sketcher::SketchObject] Sketch061
  ArcFitTolerance = 1e-06
  AttachmentSupport = -> [Pad029]
  ExternalGeometry = -> [Pad029]
  FullyConstrained = true
  MakeInternals = false
  MapMode = 5
  Placement = pos=(0,0,95) rot=(1,0,0;3.14159rad)
  sketch-geometry (1):
    g0: Circle CenterX=0 CenterY=-27.6169 CenterZ=0 NormalX=0 NormalY=0 NormalZ=1 AngleXU=0 Radius=12.5
  constraints (2):
    c: Diameter(g0) = 25
    c: Symmetric(g-3,g-3,g0)
FEATURE [PartDesign::Pocket] Pocket031
  BaseFeature = -> Pad029
  Direction = (0,0,1)
  Length = 5
  Length2 = 5
  Profile = -> Sketch061
  ReferenceAxis = -> Sketch061 [N_Axis]
  Refine = true
  Suppressed = false
  Type = 1
FEATURE [PartDesign::Fillet] Fillet003
  Base = -> Pocket031 [Edge49,Edge45]
  BaseFeature = -> Pocket031
  Radius = 2
  Refine = true
  SupportTransform = false
  Suppressed = false
  UseAllEdges = false
FEATURE [PartDesign::Fillet] Fillet004
  Base = -> Pocket030 [Face23]
  BaseFeature = -> Pocket030
  Radius = 2
  Refine = true
  SupportTransform = false
  Suppressed = false
  UseAllEdges = false
FEATURE [PartDesign::Fillet] Fillet005
  Base = -> Pocket028 [Face48]
  BaseFeature = -> Pocket028
  Radius = 1
  Refine = true
  SupportTransform = false
  Suppressed = false
  UseAllEdges = false
FEATURE [PartDesign::Fillet] Fillet006
  Base = -> Fillet003 [Face23]
  BaseFeature = -> Fillet003
  Radius = 1
  Refine = true
  SupportTransform = false
  Suppressed = false
  UseAllEdges = false
FEATURE [PartDesign::Thickness] Thickness003
  Base = -> Fillet006 [Face28]
  BaseFeature = -> Fillet006
  Intersection = true
  Join = 0
  Mode = 0
  Refine = true
  Reversed = true
  SupportTransform = false
  Suppressed = false
  Value = 2.6
FEATURE [PartDesign::Body] Body010  label="Storage Cover"
  AllowCompound = false
  Group = -> [ShapeBinder002,ShapeBinder003,Pad028,Pad029,Sketch061,Pocket031,Fillet003,Fillet006,Thickness003]
  Origin = -> Origin010
  Tip = -> Thickness003
FEATURE [PartDesign::Pocket] Pocket032
  BaseFeature = -> Fillet005
  Direction = (0,0,-1)
  Length = 2
  Length2 = 5
  Profile = -> Fillet005 [Face4]
  Refine = true
  Suppressed = false
  Type = 0
FEATURE [PartDesign::Body] Body009  label="Food Plate"
  AllowCompound = false
  Group = -> [ShapeBinder,CopyPocket017,Sketch048,Pad024,Sketch050,Sketch052,Pocket025,Thickness002,Pad025,Sketch055,Pocket026,Fillet002,Sketch058,Pad027,Sketch059,Pocket028,Fillet005,Pocket032]
  Origin = -> Origin009
  Tip = -> Pocket032
FEATURE [Sketcher::SketchObject] Sketch062
  ArcFitTolerance = 1e-06
  AttachmentSupport = -> [Pocket008]
  ExternalGeometry = -> [Pocket008]
  FullyConstrained = true
  MakeInternals = false
  MapMode = 5
  Placement = pos=(0,0,200) rot=(0,0,1;0rad)
  sketch-geometry (4):
    g0: Circle CenterX=65.69 CenterY=16.9662 CenterZ=0 NormalX=0 NormalY=0 NormalZ=1 AngleXU=0 Radius=4.25
    g1: Circle CenterX=65.69 CenterY=-59.4338 CenterZ=0 NormalX=0 NormalY=0 NormalZ=1 AngleXU=0 Radius=4.25
    g2: Circle CenterX=-67.31 CenterY=-59.4338 CenterZ=0 NormalX=0 NormalY=0 NormalZ=1 AngleXU=0 Radius=4.25
    g3: Circle CenterX=-67.31 CenterY=16.9662 CenterZ=0 NormalX=0 NormalY=0 NormalZ=1 AngleXU=0 Radius=4.25
  constraints (12):
    c: Diameter(g0) = 8.5
    c: Diameter(g1) = 8.5
    c: Diameter(g2) = 8.5
    c: Diameter(g3) = 8.5
    c: Horizontal(g1,g2)
    c: Vertical(g0,g1)
    c: Vertical(g3,g2)
    c: DistanceX(g3,g0) = 133
    c: Distance(g2,g-3) = 4.72
    c: DistanceY(g2,g3) = 76.4
    c: DistanceX(g1,g-8) = 19.31
    c: Horizontal(g3,g0)
FEATURE [PartDesign::Pocket] Pocket033
  BaseFeature = -> Pocket008
  Direction = (0,0,-1)
  Length = 5
  Length2 = 5
  Profile = -> Sketch062
  ReferenceAxis = -> Sketch062 [N_Axis]
  Refine = true
  Suppressed = false
  Type = 1
FEATURE [PartDesign::Fillet] Fillet008
  Base = -> Pocket033 [Edge120,Edge87,Edge130,Edge98]
  BaseFeature = -> Pocket033
  Radius = 1
  Refine = true
  SupportTransform = false
  Suppressed = false
  UseAllEdges = false
FEATURE [PartDesign::Body] Body  label="Food storage"
  AllowCompound = false
  Group = -> [Sketch,Pad,Fillet,Thickness,Sketch001,Pad001,Sketch003,Pad002,Pocket,Sketch004,Pocket001,Sketch009,Pocket004,DatumLine,DatumPlane,DatumPlane001,Sketch020,Pad007,Sketch021,Pad008,LinearPattern,DatumPlane002,Binder004,Pocket008,Sketch062,Pocket033,Fillet008]
  Origin = -> Origin
  Tip = -> Fillet008
FEATURE [PartDesign::ShapeBinder] ShapeBinder004  label="Screw Holes"
  Support = -> [Fillet008]
  TraceSupport = false
FEATURE [Sketcher::SketchObject] Sketch063
  ArcFitTolerance = 1e-06
  AttachmentSupport = -> [Fillet004]
  ExternalGeometry = -> [ShapeBinder004]
  FullyConstrained = true
  MakeInternals = false
  MapMode = 5
  Placement = pos=(0,0,287) rot=(1,0,0;3.14159rad)
  sketch-geometry (2):
    g0: Circle CenterX=-67.31 CenterY=59.4338 CenterZ=0 NormalX=0 NormalY=0 NormalZ=1 AngleXU=0 Radius=4.05
    g1: Circle CenterX=65.69 CenterY=59.4338 CenterZ=0 NormalX=0 NormalY=0 NormalZ=1 AngleXU=0 Radius=4.05
  constraints (4):
    c: Diameter(g0) = 8.1
    c: Coincident(g0,g-4)
    c: Diameter(g1) = 8.1
    c: Coincident(g1,g-5)
FEATURE [Sketcher::SketchObject] Sketch064
  ArcFitTolerance = 1e-06
  AttachmentSupport = -> [Fillet004]
  ExternalGeometry = -> [ShapeBinder004]
  FullyConstrained = true
  MakeInternals = false
  MapMode = 5
  Placement = pos=(0,0,225) rot=(1,0,0;3.14159rad)
  sketch-geometry (2):
    g0: Circle CenterX=-67.31 CenterY=-16.9662 CenterZ=0 NormalX=0 NormalY=0 NormalZ=1 AngleXU=0 Radius=4.05
    g1: Circle CenterX=65.69 CenterY=-16.9662 CenterZ=0 NormalX=0 NormalY=0 NormalZ=1 AngleXU=0 Radius=4.05
  constraints (4):
    c: Coincident(g0,g-4)
    c: Distance(g0,g-4) = 0.2
    c: Coincident(g1,g-3)
    c: Distance(g1,g-3) = 0.2
FEATURE [PartDesign::Pad] Pad030
  BaseFeature = -> Fillet004
  Direction = (0,0,-1)
  Length = 40
  Length2 = 10
  Profile = -> Sketch064
  ReferenceAxis = -> Sketch064 [N_Axis]
  Refine = true
  Suppressed = false
  Type = 0
FEATURE [PartDesign::Pad] Pad031
  BaseFeature = -> Pad030
  Direction = (0,0,-1)
  Length = 100
  Length2 = 10
  Profile = -> Sketch063
  ReferenceAxis = -> Sketch063 [N_Axis]
  Refine = true
  Suppressed = false
  Type = 0
FEATURE [PartDesign::Pocket] Pocket034
  BaseFeature = -> Pad031
  Direction = (0,-1,2e-16)
  Length = 12
  Length2 = 5
  Profile = -> Sketch056 [Edge3,Edge2,Edge1,Edge4]
  ReferenceAxis = -> Sketch056 [N_Axis]
  Refine = true
  Suppressed = false
  Type = 0
FEATURE [PartDesign::Body] Body006  label="Food Base"
  AllowCompound = false
  Group = -> [CopyPocket009,DatumLine001,ShapeBinder001,DatumPoint001,CopyPocket010,Pad015,Sketch034,Pocket009,Thickness001,Sketch037,Pocket010,Sketch054,Pocket024,Sketch056,Sketch057,Pad026,Pocket027,Sketch060,Pocket030,Fillet004,ShapeBinder004,Sketch063,Sketch064,Pad030,Pad031,Pocket034]
  Origin = -> Origin006
  Tip = -> Pocket034
FEATURE [App::Link] Body_CutLink
  LinkTransform = true
  LinkedObject = -> Body
FEATURE [App::Link] Body001_CutLink
  LinkTransform = true
  LinkedObject = -> Body001
FEATURE [App::Link] Body002_CutLink
  LinkTransform = true
  LinkedObject = -> Body002
FEATURE [App::Link] Body006_CutLink
  LinkTransform = true
  LinkedObject = -> Body006
FEATURE [App::Link] Body009_CutLink
  LinkTransform = true
  LinkedObject = -> Body009
FEATURE [App::Link] Body010_CutLink
  LinkTransform = true
  LinkedObject = -> Body010
FEATURE [Part::Compound] SectionCutCompound
  Links = -> [Body_CutLink,Body001_CutLink,Body002_CutLink,Body006_CutLink,Body009_CutLink,Body010_CutLink]
FEATURE [Part::Box] SectionCutBoxX
  AttacherType = Attacher::AttachEngine3D
  Height = 196
  Length = 171
  Placement = pos=(0,-72.8831,94.5) rot=(0,0,1;0rad)
  Width = 161
FEATURE [Part::Cut] SectionCutX
  Base = -> SectionCutCompound
  Refine = true
  Tool = -> SectionCutBoxX
FEATURE [Measure::MeasureLength] Length  label="Length: 87.00 mm"
  Elements = -> [SectionCutX]
  Length = 87
FEATURE [App::DocumentObjectGroup] Measurements
  Group = -> [Length]
